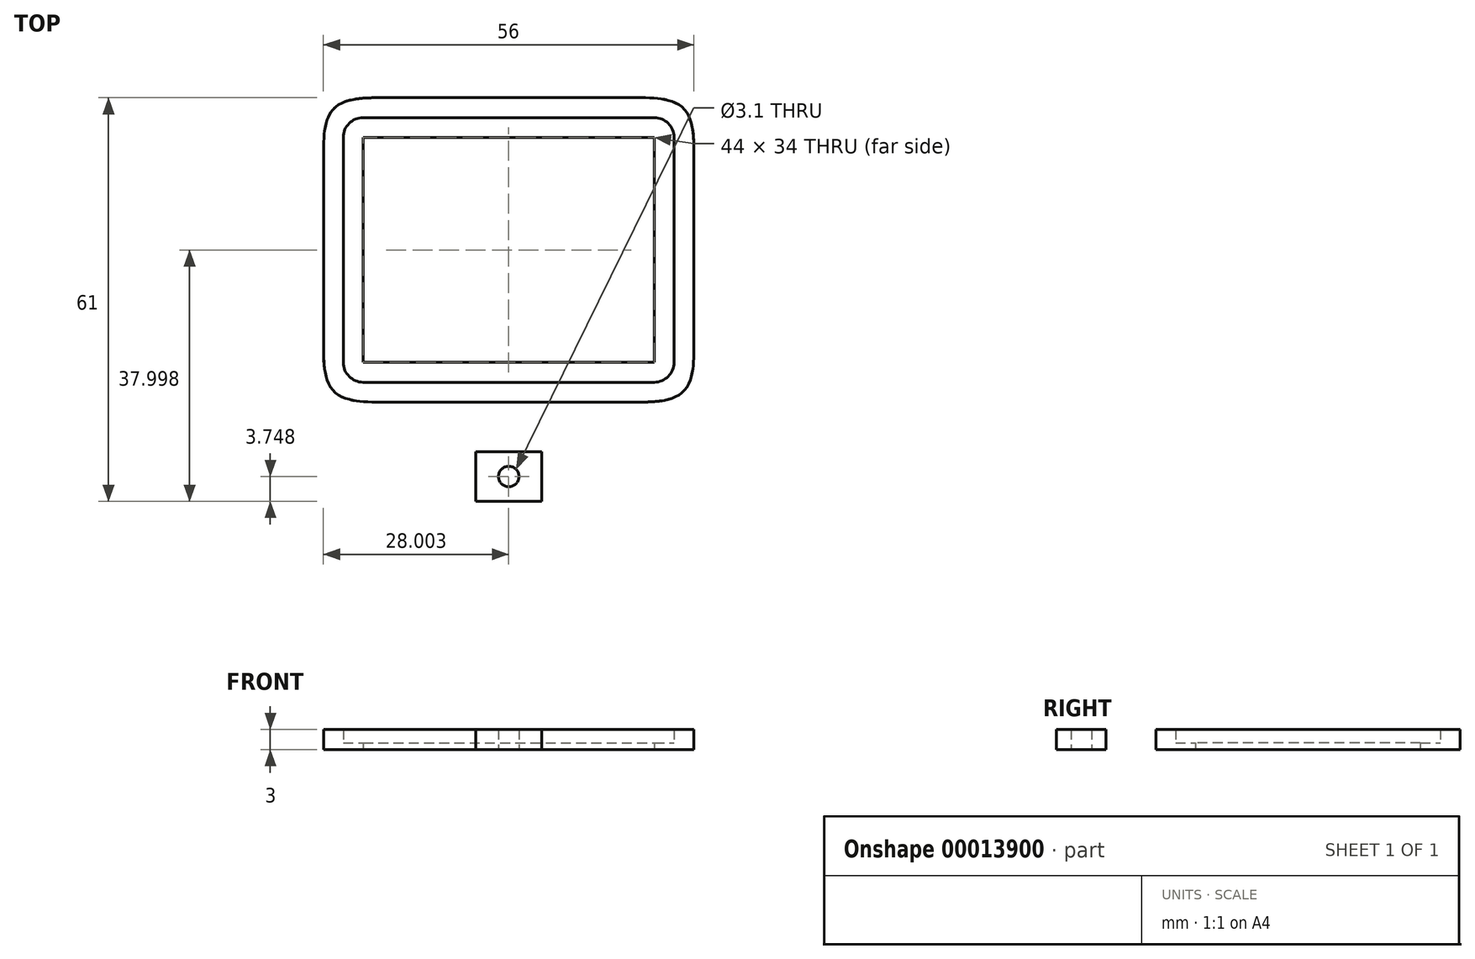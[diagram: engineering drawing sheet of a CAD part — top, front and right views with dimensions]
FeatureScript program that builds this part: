
annotation { "Feature Type Name" : "Feature", "Feature Type Description" : "" }
export const myFeature = defineFeature(function(context is Context, id is Id, definition is map)
    precondition{}
    {
        {
            var Q0;
            Q0=qCreatedBy(makeId("Top.planeOp"),FACE);
            var sketch = newSketch(context, id + "F0", { "sketchPlane" : qUnion([Q0])});
            skLineSegment(sketch, "E0.bottom", {"start": v(-22.83, 38.33) * mm, "end": v(33.17, 38.33) * mm});
            skLineSegment(sketch, "E0.top", {"start": v(-22.83, -7.67) * mm, "end": v(33.17, -7.67) * mm});
            skLineSegment(sketch, "E0.left", {"start": v(-22.83, 38.33) * mm, "end": v(-22.83, -7.67) * mm});
            skLineSegment(sketch, "E0.right", {"start": v(33.17, 38.33) * mm, "end": v(33.17, -7.67) * mm});
            skLineSegment(sketch, "E1.bottom", {"start": v(-19.83, 35.33) * mm, "end": v(30.17, 35.33) * mm});
            skLineSegment(sketch, "E1.top", {"start": v(-19.83, -4.67) * mm, "end": v(30.17, -4.67) * mm});
            skLineSegment(sketch, "E1.left", {"start": v(-19.83, 35.33) * mm, "end": v(-19.83, -4.67) * mm});
            skLineSegment(sketch, "E1.right", {"start": v(30.17, 35.33) * mm, "end": v(30.17, -4.67) * mm});
            skLineSegment(sketch, "E2.bottom", {"start": v(5.17, -7.67) * mm, "end": v(0.17, -7.67) * mm});
            skLineSegment(sketch, "E2.top", {"start": v(5.17, -22.67) * mm, "end": v(0.17, -22.67) * mm});
            skLineSegment(sketch, "E2.right", {"start": v(0.17, -7.67) * mm, "end": v(0.17, -22.67) * mm});
            skLineSegment(sketch, "E3.bottom", {"start": v(5.17, -7.67) * mm, "end": v(10.17, -7.67) * mm});
            skLineSegment(sketch, "E3.top", {"start": v(5.17, -22.67) * mm, "end": v(10.17, -22.67) * mm});
            skLineSegment(sketch, "E3.left", {"start": v(5.17, -7.67) * mm, "end": v(5.17, -15.17) * mm});
            skLineSegment(sketch, "E3.right", {"start": v(10.17, -7.67) * mm, "end": v(10.17, -22.67) * mm});
            skLineSegment(sketch, "E4", {"start": v(5.17, -15.17) * mm, "end": v(0.17, -15.17) * mm});
            skLineSegment(sketch, "E5", {"start": v(5.17, -15.17) * mm, "end": v(10.17, -15.17) * mm});
            skLineSegment(sketch, "E6", {"start": v(5.17, -15.17) * mm, "end": v(5.17, -22.67) * mm});
            skCircle(sketch, "E7", {"center": v(5.17, -11.42) * mm, "radius": 1.55 * mm});
            skCircle(sketch, "E8", {"center": v(5.17, -18.92) * mm, "radius": 1.55 * mm});
            skLineSegment(sketch, "E9.bottom", {"start": v(-16.83, 32.33) * mm, "end": v(27.17, 32.33) * mm});
            skLineSegment(sketch, "E9.top", {"start": v(-16.83, -1.67) * mm, "end": v(27.17, -1.67) * mm});
            skLineSegment(sketch, "E9.left", {"start": v(-16.83, 32.33) * mm, "end": v(-16.83, -1.67) * mm});
            skLineSegment(sketch, "E9.right", {"start": v(27.17, 32.33) * mm, "end": v(27.17, -1.67) * mm});
            skSolve(sketch);
        }
        {
            var Q0;
            Q0=makeQuery(id+"F0.imprint","IMPRINT",FACE,{"disambiguationData":[TD([[makeQuery(id+"F0.imprint","IMPRINT",EDGE,{"derivedFrom":sQuery(id+"F0.wireOp",EDGE,"E0.bottom")}),-1.0]])]});
            var Q1;
            {var subQ5=sQuery(id+"F0.wireOp",EDGE,"E2.bottom");Q1=makeQuery(id+"F0.imprint","IMPRINT",FACE,{"disambiguationData":[TD([[makeQuery(id+"F0.imprint","IMPRINT",EDGE,{"derivedFrom":subQ5}),1.0]])]});}
            var Q2;
            {var subQ6=sQuery(id+"F0.wireOp",EDGE,"E3.bottom");Q2=makeQuery(id+"F0.imprint","IMPRINT",FACE,{"disambiguationData":[TD([[makeQuery(id+"F0.imprint","IMPRINT",EDGE,{"derivedFrom":subQ6}),-1.0]])]});}
            var Q3;
            {var subQ4=sQuery(id+"F0.wireOp",EDGE,"E3.top");Q3=makeQuery(id+"F0.imprint","IMPRINT",FACE,{"disambiguationData":[TD([[makeQuery(id+"F0.imprint","IMPRINT",EDGE,{"derivedFrom":subQ4}),1.0]])]});}
            var Q4;
            {var subQ4=sQuery(id+"F0.wireOp",EDGE,"E2.top");Q4=makeQuery(id+"F0.imprint","IMPRINT",FACE,{"disambiguationData":[TD([[makeQuery(id+"F0.imprint","IMPRINT",EDGE,{"derivedFrom":subQ4}),-1.0]])]});}
            extrude(context, id + "F1", {"entities" : qUnion([Q0, Q1, Q2, Q3, Q4]), "depth" : 3 * mm});
        }
        {
            var Q0;
            Q0=makeQuery(id+"F1.opExtrude","SWEPT_EDGE",EDGE,{"disambiguationData":[OSD([sQuery(id+"F0.wireOp",EDGE,"E0.top"),sQuery(id+"F0.wireOp",EDGE,"E0.left")])]});
            var Q1;
            Q1=makeQuery(id+"F1.opExtrude","SWEPT_EDGE",EDGE,{"disambiguationData":[OSD([sQuery(id+"F0.wireOp",EDGE,"E0.bottom"),sQuery(id+"F0.wireOp",EDGE,"E0.left")])]});
            var Q2;
            Q2=makeQuery(id+"F1.opExtrude","SWEPT_EDGE",EDGE,{"disambiguationData":[OSD([sQuery(id+"F0.wireOp",EDGE,"E0.top"),sQuery(id+"F0.wireOp",EDGE,"E0.right")])]});
            var Q3;
            Q3=makeQuery(id+"F1.opExtrude","SWEPT_EDGE",EDGE,{"disambiguationData":[OSD([sQuery(id+"F0.wireOp",EDGE,"E0.bottom"),sQuery(id+"F0.wireOp",EDGE,"E0.right")])]});
            fillet(context, id + "F2", {"entities" : qUnion([Q0, Q1, Q2, Q3]), "radius" : 8 * mm, "rho" : 0.6, "crossSection" : FilletCrossSection.CONIC, "allowEdgeOverflow" : false});
        }
        {
            var Q0;
            Q0=makeQuery(id+"F1.opExtrude","SWEPT_EDGE",EDGE,{"disambiguationData":[OSD([sQuery(id+"F0.wireOp",EDGE,"E1.bottom"),sQuery(id+"F0.wireOp",EDGE,"E1.left")])]});
            var Q1;
            Q1=makeQuery(id+"F1.opExtrude","SWEPT_EDGE",EDGE,{"disambiguationData":[OSD([sQuery(id+"F0.wireOp",EDGE,"E1.top"),sQuery(id+"F0.wireOp",EDGE,"E1.left")])]});
            var Q2;
            Q2=makeQuery(id+"F1.opExtrude","SWEPT_EDGE",EDGE,{"disambiguationData":[OSD([sQuery(id+"F0.wireOp",EDGE,"E1.bottom"),sQuery(id+"F0.wireOp",EDGE,"E1.right")])]});
            var Q3;
            Q3=makeQuery(id+"F1.opExtrude","SWEPT_EDGE",EDGE,{"disambiguationData":[OSD([sQuery(id+"F0.wireOp",EDGE,"E1.top"),sQuery(id+"F0.wireOp",EDGE,"E1.right")])]});
            fillet(context, id + "F3", {"entities" : qUnion([Q0, Q1, Q2, Q3]), "radius" : 3 * mm, "tangentPropagation" : true, "allowEdgeOverflow" : false});
        }
        {
            var Q0;
            Q0=makeQuery(id+"F0.imprint","IMPRINT",FACE,{"disambiguationData":[TD([[makeQuery(id+"F0.imprint","IMPRINT",EDGE,{"derivedFrom":sQuery(id+"F0.wireOp",EDGE,"E1.bottom")}),-1.0]])]});
            extrude(context, id + "F4", {"entities" : qUnion([Q0]), "operationType" : NewBodyOperationType.ADD, "depth" : 1 * mm});
        }
    });
